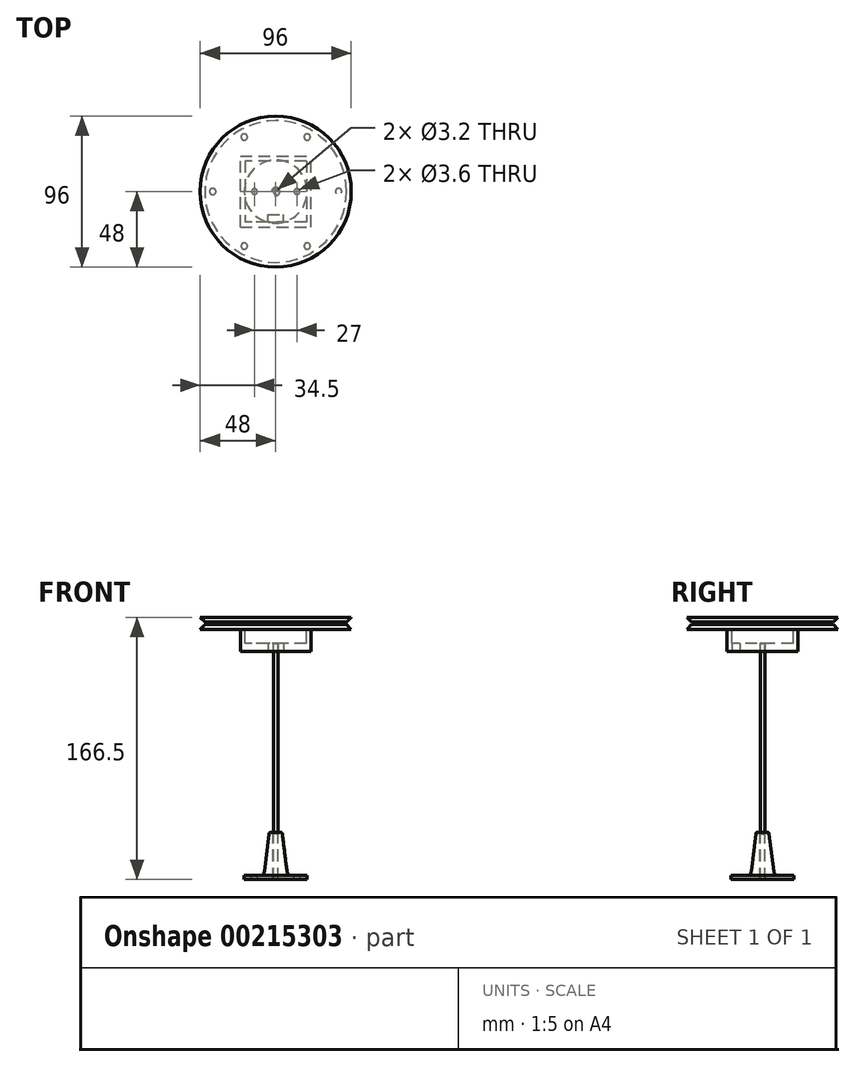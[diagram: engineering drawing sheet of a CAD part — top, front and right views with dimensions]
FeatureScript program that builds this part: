
annotation { "Feature Type Name" : "Feature", "Feature Type Description" : "" }
export const myFeature = defineFeature(function(context is Context, id is Id, definition is map)
    precondition{}
    {
        {
            var Q0;
            Q0=qCreatedBy(makeId("Top.planeOp"),FACE);
            var sketch = newSketch(context, id + "F0", { "sketchPlane" : qUnion([Q0])});
            skCircle(sketch, "E0", {"center": v(0, 0) * mm, "radius": 45 * mm});
            skSolve(sketch);
        }
        {
            var Q0;
            Q0 = qSketchRegion(id + "F0", true);
            extrude(context, id + "F1", {"entities" : qUnion([Q0]), "depth" : 3 * mm, "hasDraft" : true, "draftAngle" : 45 * degree});
        }
        {
            var Q0;
            Q0=makeQuery(id+"F1.opExtrude","CAP_FACE",FACE,{"disambiguationData":[OSD([sQuery(id+"F0.wireOp",EDGE,"E0")])],"isStart":true});
            var sketch = newSketch(context, id + "F2", { "sketchPlane" : qUnion([Q0])});
            skCircle(sketch, "E1", {"center": v(40, 0) * mm, "radius": 2 * mm});
            skCircle(sketch, "E2.1.0", {"center": v(20, 34.64) * mm, "radius": 2 * mm});
            skCircle(sketch, "E2.2.0", {"center": v(-20, 34.64) * mm, "radius": 2 * mm});
            skCircle(sketch, "E2.3.0", {"center": v(-40, 0) * mm, "radius": 2 * mm});
            skCircle(sketch, "E2.4.0", {"center": v(-20, -34.64) * mm, "radius": 2 * mm});
            skCircle(sketch, "E2.5.0", {"center": v(20, -34.64) * mm, "radius": 2 * mm});
            skPoint(sketch, "E2.center", {"position": v(0, 0) * mm});
            skSolve(sketch);
        }
        {
            var Q0;
            Q0 = qSketchRegion(id + "F2", true);
            extrude(context, id + "F3", {"entities" : qUnion([Q0]), "operationType" : NewBodyOperationType.ADD, "depth" : 1.5 * mm});
        }
        {
            var Q0;
            Q0=makeQuery(id+"F3.opExtrude","CAP_FACE",FACE,{"disambiguationData":[OSD([sQuery(id+"F2.wireOp",EDGE,"E2.3.0")])],"isStart":false});
            var sketch = newSketch(context, id + "F4", { "sketchPlane" : qUnion([Q0])});
            skCircle(sketch, "E3.0", {"center": v(0, 0) * mm, "radius": 45 * mm});
            skSolve(sketch);
        }
        {
            var Q0;
            Q0 = qSketchRegion(id + "F4", true);
            extrude(context, id + "F5", {"entities" : qUnion([Q0]), "depth" : 3 * mm, "hasDraft" : true, "draftAngle" : 45 * degree});
        }
        {
            var Q0;
            Q0=makeQuery(id+"F5.opExtrude","CAP_FACE",FACE,{"disambiguationData":[OSD([sQuery(id+"F4.wireOp",EDGE,"E3.0")])],"isStart":true});
            var sketch = newSketch(context, id + "F6", { "sketchPlane" : qUnion([Q0])});
            skLineSegment(sketch, "E4.bottom", {"start": v(22.5, 22.5) * mm, "end": v(-22.5, 22.5) * mm});
            skLineSegment(sketch, "E4.top", {"start": v(22.5, -22.5) * mm, "end": v(-22.5, -22.5) * mm});
            skLineSegment(sketch, "E4.left", {"start": v(22.5, 22.5) * mm, "end": v(22.5, -22.5) * mm});
            skLineSegment(sketch, "E4.right", {"start": v(-22.5, 22.5) * mm, "end": v(-22.5, -22.5) * mm});
            skPoint(sketch, "E4.middle", {"position": v(0, 0) * mm});
            skSolve(sketch);
        }
        {
            var Q0;
            Q0 = qSketchRegion(id + "F6", true);
            extrude(context, id + "F7", {"entities" : qUnion([Q0]), "operationType" : NewBodyOperationType.ADD, "oppositeDirection" : true, "depth" : 17 * mm});
        }
        {
            var Q0;
            Q0=makeQuery(id+"F6.imprint","IMPRINT",FACE,{"disambiguationData":[TD([[makeQuery(id+"F6.imprint","IMPRINT",EDGE,{"derivedFrom":sQuery(id+"F6.wireOp",EDGE,"E4.bottom")}),1.0]])]});
            var sketch = newSketch(context, id + "F8", { "sketchPlane" : qUnion([Q0])});
            skLineSegment(sketch, "E5.0", {"start": v(19.5, 19.5) * mm, "end": v(-19.5, 19.5) * mm});
            skLineSegment(sketch, "E5.1", {"start": v(19.5, 19.5) * mm, "end": v(19.5, -19.5) * mm});
            skLineSegment(sketch, "E5.2", {"start": v(19.5, -19.5) * mm, "end": v(-19.5, -19.5) * mm});
            skLineSegment(sketch, "E5.3", {"start": v(-19.5, 19.5) * mm, "end": v(-19.5, -19.5) * mm});
            skSolve(sketch);
        }
        {
            var Q0;
            Q0=makeQuery(id+"F7.opExtrude","CAP_FACE",FACE,{"disambiguationData":[OSD([sQuery(id+"F6.wireOp",EDGE,"E4.bottom"),sQuery(id+"F6.wireOp",EDGE,"E4.top"),sQuery(id+"F6.wireOp",EDGE,"E4.left"),sQuery(id+"F6.wireOp",EDGE,"E4.right")])],"isStart":false});
            cPlane(context, id + "F9", {"entities" : qUnion([Q0]), "cplaneType" : CPlaneType.OFFSET, "offset" : 5 * mm, "oppositeDirection" : true, "width" : 150 * mm, "height" : 150 * mm});
        }
        {
            var Q0;
            Q0 = qSketchRegion(id + "F8", true);
            var Q1;
            Q1=qCreatedBy(id+"F9.planeOp",FACE);
            extrude(context, id + "F10", {"entities" : qUnion([Q0]), "operationType" : NewBodyOperationType.REMOVE, "endBound" : BoundingType.UP_TO_SURFACE, "oppositeDirection" : true, "endBoundEntityFace" : qUnion([Q1]), "depth" : 25 * mm});
        }
        {
            var Q0;
            Q0=makeQuery(id+"F7.opExtrude","CAP_FACE",FACE,{"disambiguationData":[OSD([sQuery(id+"F6.wireOp",EDGE,"E4.bottom"),sQuery(id+"F6.wireOp",EDGE,"E4.top"),sQuery(id+"F6.wireOp",EDGE,"E4.left"),sQuery(id+"F6.wireOp",EDGE,"E4.right")])],"isStart":false});
            var sketch = newSketch(context, id + "F11", { "sketchPlane" : qUnion([Q0])});
            skLineSegment(sketch, "E6.bottom", {"start": v(-5, 19.5) * mm, "end": v(5, 19.5) * mm});
            skLineSegment(sketch, "E6.top", {"start": v(-5, 14.5) * mm, "end": v(5, 14.5) * mm});
            skLineSegment(sketch, "E6.left", {"start": v(-5, 19.5) * mm, "end": v(-5, 14.5) * mm});
            skLineSegment(sketch, "E6.right", {"start": v(5, 19.5) * mm, "end": v(5, 14.5) * mm});
            skLineSegment(sketch, "E7.0", {"start": v(19.5, 19.5) * mm, "end": v(-19.5, 19.5) * mm, "construction": true});
            skLineSegment(sketch, "E8", {"start": v(0, 19.5) * mm, "end": v(0, 14.5) * mm, "construction": true});
            skCircle(sketch, "E9", {"center": v(0, 0) * mm, "radius": 1.6 * mm});
            skSolve(sketch);
        }
        {
            var Q0;
            Q0 = qSketchRegion(id + "F11", true);
            extrude(context, id + "F12", {"entities" : qUnion([Q0]), "operationType" : NewBodyOperationType.REMOVE, "endBound" : BoundingType.UP_TO_NEXT, "oppositeDirection" : true, "depth" : 25 * mm});
        }
        {
            var Q0;
            Q0=qCreatedBy(id+"F9.planeOp",FACE);
            var sketch = newSketch(context, id + "F13", { "sketchPlane" : qUnion([Q0])});
            skCircle(sketch, "E10", {"center": v(0, 0) * mm, "radius": 1.5 * mm});
            skSolve(sketch);
        }
        {
            var Q0;
            Q0 = qSketchRegion(id + "F13", true);
            extrude(context, id + "F14", {"entities" : qUnion([Q0]), "depth" : 150 * mm});
        }
        {
            var Q0;
            Q0=qCreatedBy(makeId("Right.planeOp"),FACE);
            var sketch = newSketch(context, id + "F15", { "sketchPlane" : qUnion([Q0])});
            skLineSegment(sketch, "E11", {"start": v(-20, -163.5) * mm, "end": v(-1.6, -163.5) * mm});
            skLineSegment(sketch, "E12", {"start": v(-1.6, -163.5) * mm, "end": v(-1.6, -133.5) * mm});
            skLineSegment(sketch, "E13", {"start": v(0, 0) * mm, "end": v(0, -169.56) * mm, "construction": true});
            skLineSegment(sketch, "E14", {"start": v(-1.6, -133.5) * mm, "end": v(-4.1, -133.5) * mm});
            skLineSegment(sketch, "E15", {"start": v(-4.1, -133.5) * mm, "end": v(-7.5, -161) * mm});
            skLineSegment(sketch, "E16", {"start": v(-20, -163.5) * mm, "end": v(-20, -161) * mm});
            skLineSegment(sketch, "E17", {"start": v(-20, -161) * mm, "end": v(-7.5, -161) * mm});
            skSolve(sketch);
        }
        {
            var Q0;
            Q0=makeQuery(id+"F15.imprint","IMPRINT",FACE,{"disambiguationData":[TD([[makeQuery(id+"F15.imprint","IMPRINT",EDGE,{"derivedFrom":sQuery(id+"F15.wireOp",EDGE,"E11")}),1.0]])]});
            var Q1;
            Q1=sQuery(id+"F15.wireOp",EDGE,"0EkMlOQg-qWuT-JLqA-7Ehd-94k4hTO6Vzyv");
            var Q2;
            Q2=sQuery(id+"F15.wireOp",EDGE,"KyyuDjum-0ACa-CiF6-VySb-TIYCSIet2goH");
            var Q3;
            Q3=sQuery(id+"F15.wireOp",EDGE,"REXbUgf8-2IhL-a8TU-M0Vd-YKJtHhvMTGbu");
            var Q4;
            Q4=sQuery(id+"F15.wireOp",EDGE,"yp53QtNE-deFQ-UkDs-jM9g-v7ZKnORVGwSl");
            var Q5;
            Q5=sQuery(id+"F15.wireOp",EDGE,"5CRnWVjS-5UB7-EG8S-ikPh-JkE33K7GkA7x");
            var Q6;
            Q6=sQuery(id+"F15.wireOp",EDGE,"uP2YRY1S-BXEW-1PDN-pkdV-0HkFVv7BHLgk");
            var Q7;
            Q7=sQuery(id+"F15.wireOp",EDGE,"E13");
            revolve(context, id + "F16", {"entities" : qUnion([Q0]), "surfaceEntities" : qUnion([Q1, Q2, Q3, Q4, Q5, Q6]), "axis" : qUnion([Q7]), "revolveType" : RevolveType.FULL});
        }
        {
            var Q0;
            Q0=makeQuery(id+"F16.opRevolve","SWEPT_FACE",FACE,{"disambiguationData":[OSD([sQuery(id+"F15.wireOp",EDGE,"E17")])]});
            var sketch = newSketch(context, id + "F17", { "sketchPlane" : qUnion([Q0])});
            skCircle(sketch, "E18", {"center": v(13.5, 0) * mm, "radius": 1.8 * mm});
            skCircle(sketch, "E19", {"center": v(-13.5, 0) * mm, "radius": 1.8 * mm});
            skLineSegment(sketch, "E20", {"start": v(-13.5, 0) * mm, "end": v(0, 0) * mm, "construction": true});
            skLineSegment(sketch, "E21", {"start": v(0, 0) * mm, "end": v(13.5, 0) * mm, "construction": true});
            skSolve(sketch);
        }
        {
            var Q0;
            Q0 = qSketchRegion(id + "F17", true);
            extrude(context, id + "F18", {"entities" : qUnion([Q0]), "operationType" : NewBodyOperationType.REMOVE, "endBound" : BoundingType.THROUGH_ALL, "oppositeDirection" : true, "depth" : 25 * mm});
        }
        {
            var Q0;
            Q0=makeQuery(id+"F16.opRevolve","SWEPT_EDGE",EDGE,{"disambiguationData":[OSD([sQuery(id+"F15.wireOp",EDGE,"E15"),sQuery(id+"F15.wireOp",EDGE,"E17")])]});
            fillet(context, id + "F19", {"entities" : qUnion([Q0]), "radius" : 3 * mm, "tangentPropagation" : true, "allowEdgeOverflow" : false});
        }
        {
            var Q0;
            Q0=makeQuery(id+"F16.opRevolve","SWEPT_EDGE",EDGE,{"disambiguationData":[OSD([sQuery(id+"F15.wireOp",EDGE,"E12"),sQuery(id+"F15.wireOp",EDGE,"E14")])]});
            chamfer(context, id + "F20", {"entities" : qUnion([Q0]), "width" : 1 * mm, "tangentPropagation" : true});
        }
        {
            var Q0;
            Q0=makeQuery(id+"F16.opRevolve","SWEPT_EDGE",EDGE,{"disambiguationData":[OSD([sQuery(id+"F15.wireOp",EDGE,"E14"),sQuery(id+"F15.wireOp",EDGE,"E15")])]});
            fillet(context, id + "F21", {"entities" : qUnion([Q0]), "radius" : 1 * mm, "tangentPropagation" : true, "allowEdgeOverflow" : false});
        }
    });
